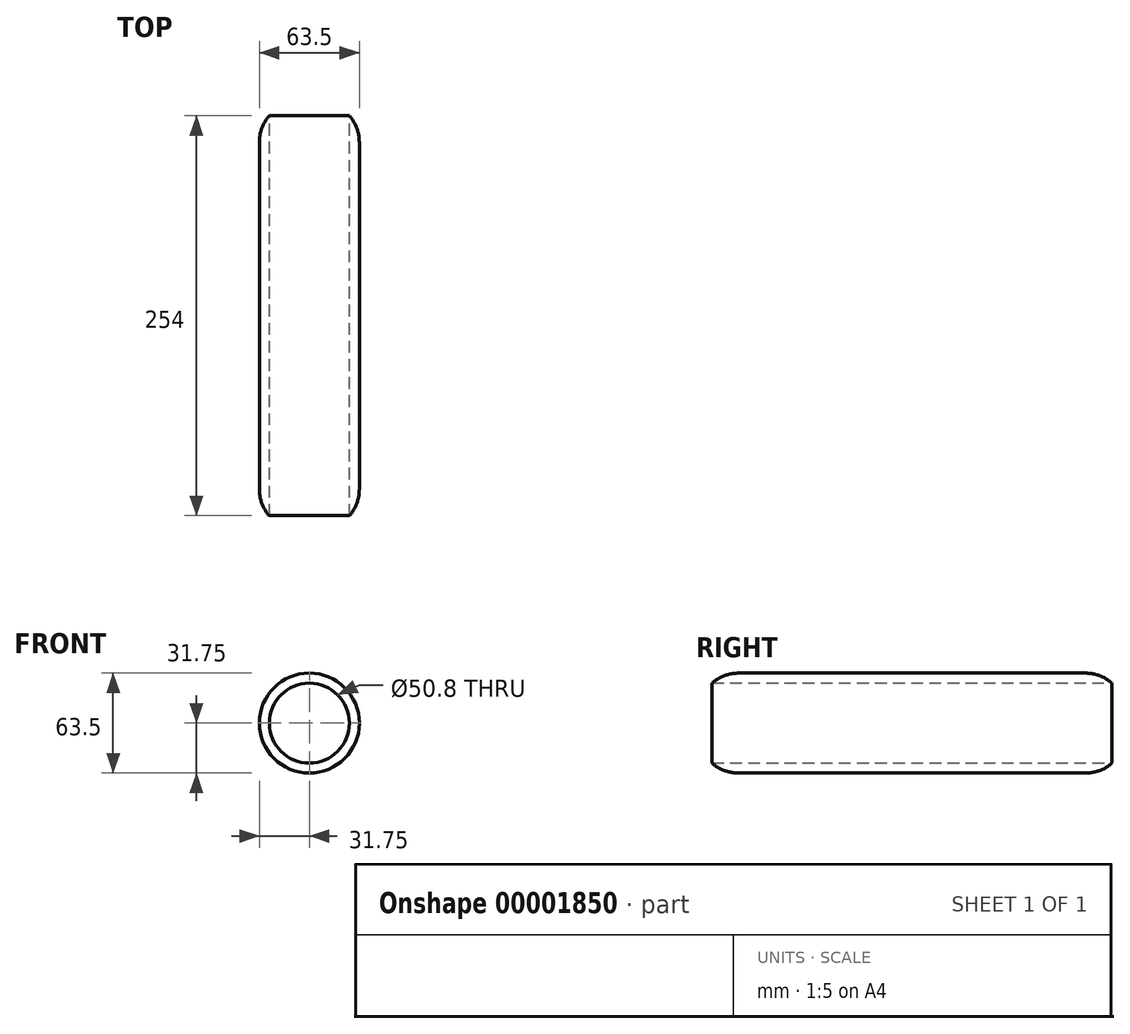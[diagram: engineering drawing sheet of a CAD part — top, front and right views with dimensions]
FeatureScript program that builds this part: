
annotation { "Feature Type Name" : "Feature", "Feature Type Description" : "" }
export const myFeature = defineFeature(function(context is Context, id is Id, definition is map)
    precondition{}
    {
        {
            var Q0;
            Q0=qCreatedBy(makeId("Front.planeOp"),FACE);
            var sketch = newSketch(context, id + "F0", { "sketchPlane" : qUnion([Q0])});
            skCircle(sketch, "E0", {"center": v(0, 0) * mm, "radius": 31.75 * mm});
            skCircle(sketch, "E1", {"center": v(0, 0) * mm, "radius": 25.4 * mm});
            skSolve(sketch);
        }
        {
            var Q0;
            Q0 = qSketchRegion(id + "F0", true);
            extrude(context, id + "F1", {"entities" : qUnion([Q0]), "endBound" : BoundingType.SYMMETRIC, "depth" : 254 * mm});
        }
        {
            var Q0;
            Q0=makeQuery(id+"F1.opExtrude","CAP_EDGE",EDGE,{"disambiguationData":[OSD([sQuery(id+"F0.wireOp",EDGE,"E0")])],"isStart":false});
            var Q1;
            Q1=makeQuery(id+"F1.opExtrude","CAP_EDGE",EDGE,{"disambiguationData":[OSD([sQuery(id+"F0.wireOp",EDGE,"E0")])],"isStart":true});
            fillet(context, id + "F2", {"entities" : qUnion([Q0, Q1]), "radius" : 25.4 * mm, "tangentPropagation" : true, "allowEdgeOverflow" : false});
        }
    });
